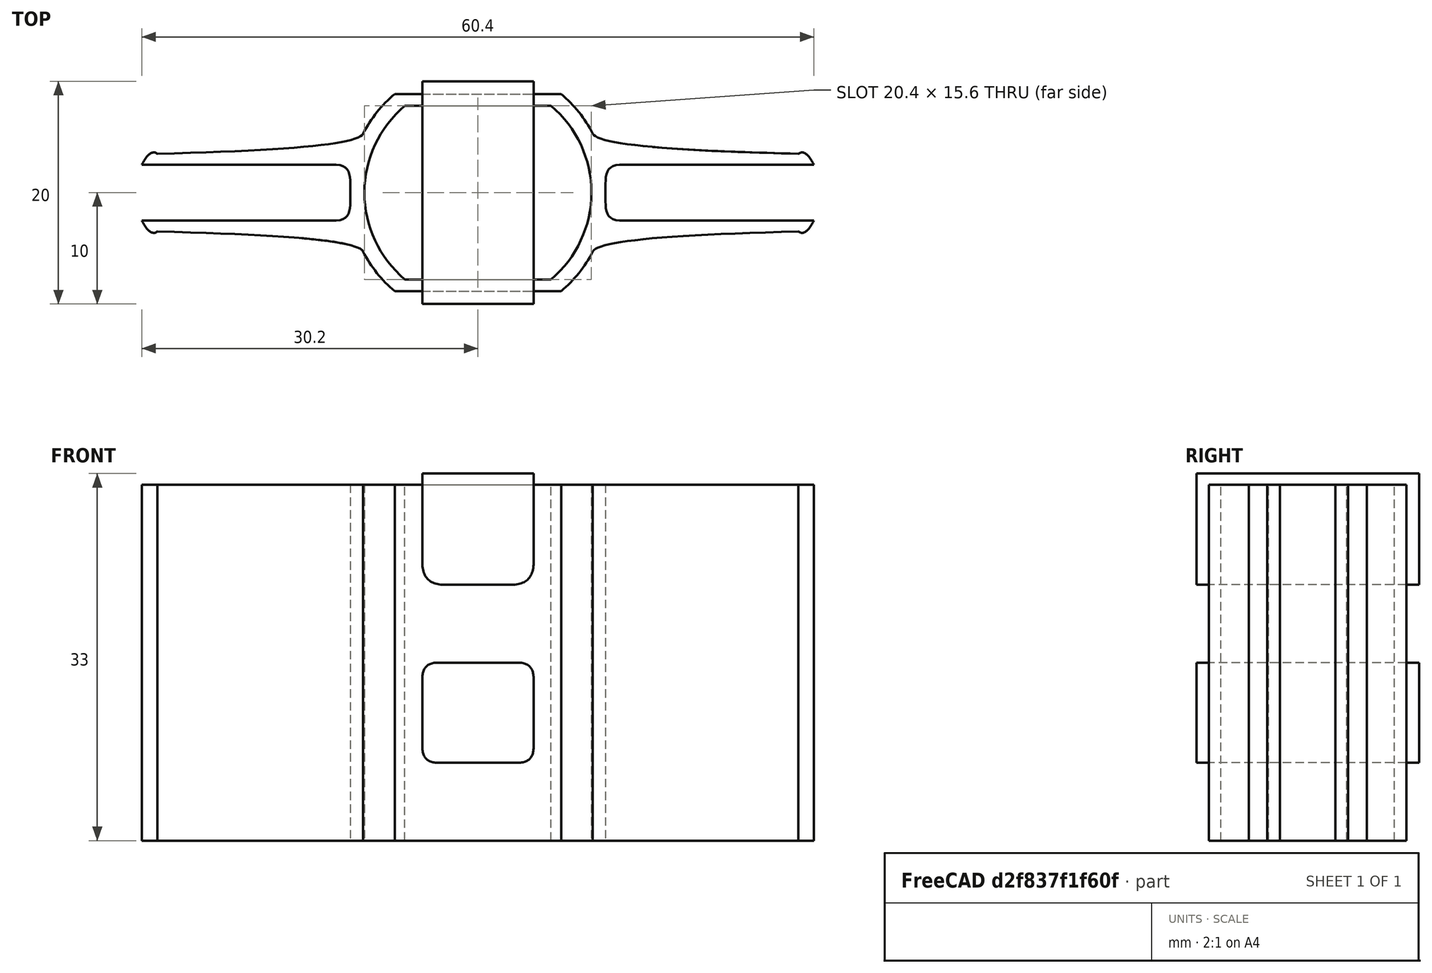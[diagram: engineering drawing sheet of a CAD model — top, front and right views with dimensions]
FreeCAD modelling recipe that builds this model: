
FCSTD DOCUMENT  (FreeCAD 0.19R0.19.2)
Label: 021
License: All rights reserved
LicenseURL: http://en.wikipedia.org/wiki/All_rights_reserved
objects: Sketcher::SketchObject×3, Part::Extrusion×2
note: 5 computed .brp shape members not serialized (recipe doc carries the construction recipe); baked Part::Feature solids carry a one-line shape summary decoded from their .brp

FEATURE [Sketcher::SketchObject] Sketch  label="main001"
  FullyConstrained = true
  sketch-geometry (80):
    g0: ArcOfCircle CenterX=-3.45031e-07 CenterY=0 CenterZ=0 NormalX=0 NormalY=0 NormalZ=1 AngleXU=0 Radius=10.2 StartAngle=5.4126 EndAngle=7.15377
    g1: ArcOfCircle CenterX=-3.45031e-07 CenterY=0 CenterZ=0 NormalX=0 NormalY=0 NormalZ=1 AngleXU=0 Radius=10.2 StartAngle=2.27101 EndAngle=4.01218
    g2: LineSegment StartX=-6.57267 StartY=7.8 StartZ=0 EndX=6.57267 EndY=7.8 EndZ=0
    g3: LineSegment StartX=-6.57267 StartY=-7.8 StartZ=0 EndX=6.57267 EndY=-7.8 EndZ=0
    g4: ArcOfCircle CenterX=-3.45031e-07 CenterY=0 CenterZ=0 NormalX=0 NormalY=0 NormalZ=1 AngleXU=0 Radius=11.6 StartAngle=2.27101 EndAngle=2.66709
    g5: ArcOfCircle CenterX=-3.45031e-07 CenterY=0 CenterZ=0 NormalX=0 NormalY=0 NormalZ=1 AngleXU=0 Radius=11.6 StartAngle=5.4126 EndAngle=5.80868
    g6: LineSegment StartX=-7.4748 StartY=8.87059 StartZ=0 EndX=7.4748 EndY=8.87059 EndZ=0
    g7: LineSegment StartX=-7.4748 StartY=-8.87059 StartZ=0 EndX=7.4748 EndY=-8.87059 EndZ=0
    g8: ArcOfCircle CenterX=-3.45031e-07 CenterY=0 CenterZ=0 NormalX=0 NormalY=0 NormalZ=1 AngleXU=0 Radius=11.6 StartAngle=3.6161 EndAngle=4.01218
    g9: ArcOfCircle CenterX=-3.45031e-07 CenterY=0 CenterZ=0 NormalX=0 NormalY=0 NormalZ=1 AngleXU=0 Radius=11.6 StartAngle=0.474503 EndAngle=0.870585
    g10: Circle CenterX=-28.8 CenterY=3.5 CenterZ=0 NormalX=0 NormalY=0 NormalZ=1 AngleXU=0 Radius=1
    g11: Circle CenterX=-10.9247 CenterY=3.9 CenterZ=0 NormalX=0 NormalY=0 NormalZ=1 AngleXU=0 Radius=1
    g12: Circle CenterX=-10.3184 CenterY=5.3 CenterZ=0 NormalX=0 NormalY=0 NormalZ=1 AngleXU=0 Radius=1
    g13: BSplineCurve PolesCount=3 KnotsCount=2 Degree=2 IsPeriodic=0
    g14: GeomPoint X=-28.8 Y=3.5 Z=0
    g15: GeomPoint X=-10.3184 Y=5.3 Z=0
    g16: Circle CenterX=28.8 CenterY=3.5 CenterZ=0 NormalX=0 NormalY=0 NormalZ=1 AngleXU=0 Radius=1
    g17: Circle CenterX=10.9247 CenterY=3.9 CenterZ=0 NormalX=0 NormalY=0 NormalZ=1 AngleXU=0 Radius=1
    g18: Circle CenterX=10.3184 CenterY=5.3 CenterZ=0 NormalX=0 NormalY=0 NormalZ=1 AngleXU=0 Radius=1
    g19: BSplineCurve PolesCount=3 KnotsCount=2 Degree=2 IsPeriodic=0
    g20: GeomPoint X=28.8 Y=3.5 Z=0
    g21: GeomPoint X=10.3184 Y=5.3 Z=0
    g22: Circle CenterX=-28.8 CenterY=-3.5 CenterZ=0 NormalX=0 NormalY=0 NormalZ=1 AngleXU=0 Radius=1
    g23: Circle CenterX=-10.9247 CenterY=-3.9 CenterZ=0 NormalX=0 NormalY=0 NormalZ=1 AngleXU=0 Radius=1
    g24: Circle CenterX=-10.3184 CenterY=-5.3 CenterZ=0 NormalX=0 NormalY=0 NormalZ=1 AngleXU=0 Radius=1
    g25: BSplineCurve PolesCount=3 KnotsCount=2 Degree=2 IsPeriodic=0
    g26: GeomPoint X=-28.8 Y=-3.5 Z=0
    g27: GeomPoint X=-10.3184 Y=-5.3 Z=0
    g28: Circle CenterX=28.8 CenterY=-3.5 CenterZ=0 NormalX=0 NormalY=0 NormalZ=1 AngleXU=0 Radius=1
    g29: Circle CenterX=10.9247 CenterY=-3.9 CenterZ=0 NormalX=0 NormalY=0 NormalZ=1 AngleXU=0 Radius=1
    g30: Circle CenterX=10.3184 CenterY=-5.3 CenterZ=0 NormalX=0 NormalY=0 NormalZ=1 AngleXU=0 Radius=1
    g31: BSplineCurve PolesCount=3 KnotsCount=2 Degree=2 IsPeriodic=0
    g32: GeomPoint X=28.8 Y=-3.5 Z=0
    g33: GeomPoint X=10.3184 Y=-5.3 Z=0
    g34-g38: Circle x5 (B-spline internal-alignment scaffolding for g39; pole/knot coordinates omitted)
    g39: BSplineCurve PolesCount=5 KnotsCount=3 Degree=3 IsPeriodic=0
    g40: GeomPoint X=12.7274 Y=2.5 Z=0
    g41: GeomPoint X=11.4637 Y=2.49999e-07 Z=0
    g42: GeomPoint X=12.7274 Y=-2.5 Z=0
    g43-g47: Circle x5 (B-spline internal-alignment scaffolding for g48; pole/knot coordinates omitted)
    g48: BSplineCurve PolesCount=5 KnotsCount=3 Degree=3 IsPeriodic=0
    g49: GeomPoint X=-12.7274 Y=2.5 Z=0
    g50: GeomPoint X=-11.4637 Y=2.50004e-07 Z=0
    g51: GeomPoint X=-12.7274 Y=-2.5 Z=0
    g52: LineSegment StartX=-30.2 StartY=-2.5 StartZ=0 EndX=-12.7274 EndY=-2.5 EndZ=0
    g53: LineSegment StartX=-30.2 StartY=2.5 StartZ=0 EndX=-12.7274 EndY=2.5 EndZ=0
    g54: LineSegment StartX=30.2 StartY=2.5 StartZ=0 EndX=12.7274 EndY=2.5 EndZ=0
    g55: LineSegment StartX=30.2 StartY=-2.5 StartZ=0 EndX=12.7274 EndY=-2.5 EndZ=0
    g56: Circle CenterX=-30.2 CenterY=2.5 CenterZ=0 NormalX=0 NormalY=0 NormalZ=1 AngleXU=0 Radius=1
    g57: Circle CenterX=-29.4304 CenterY=3.99253 CenterZ=0 NormalX=0 NormalY=0 NormalZ=1 AngleXU=0 Radius=1
    g58: Circle CenterX=-28.8 CenterY=3.5 CenterZ=0 NormalX=0 NormalY=0 NormalZ=1 AngleXU=0 Radius=1
    g59: BSplineCurve PolesCount=3 KnotsCount=2 Degree=2 IsPeriodic=0
    g60: GeomPoint X=-30.2 Y=2.5 Z=0
    g61: GeomPoint X=-28.8 Y=3.5 Z=0
    g62: Circle CenterX=30.2 CenterY=-2.5 CenterZ=0 NormalX=0 NormalY=0 NormalZ=1 AngleXU=0 Radius=1
    g63: Circle CenterX=29.4304 CenterY=-3.99253 CenterZ=0 NormalX=0 NormalY=0 NormalZ=1 AngleXU=0 Radius=1
    g64: Circle CenterX=28.8 CenterY=-3.5 CenterZ=0 NormalX=0 NormalY=0 NormalZ=1 AngleXU=0 Radius=1
    g65: BSplineCurve PolesCount=3 KnotsCount=2 Degree=2 IsPeriodic=0
    g66: GeomPoint X=30.2 Y=-2.5 Z=0
    g67: GeomPoint X=28.8 Y=-3.5 Z=0
    g68: Circle CenterX=30.2 CenterY=2.5 CenterZ=0 NormalX=0 NormalY=0 NormalZ=1 AngleXU=0 Radius=1
    g69: Circle CenterX=29.4304 CenterY=3.99253 CenterZ=0 NormalX=0 NormalY=0 NormalZ=1 AngleXU=0 Radius=1
    g70: Circle CenterX=28.8 CenterY=3.5 CenterZ=0 NormalX=0 NormalY=0 NormalZ=1 AngleXU=0 Radius=1
    g71: BSplineCurve PolesCount=3 KnotsCount=2 Degree=2 IsPeriodic=0
    g72: GeomPoint X=30.2 Y=2.5 Z=0
    g73: GeomPoint X=28.8 Y=3.5 Z=0
    g74: Circle CenterX=-30.2 CenterY=-2.5 CenterZ=0 NormalX=0 NormalY=0 NormalZ=1 AngleXU=0 Radius=1
    g75: Circle CenterX=-29.4304 CenterY=-3.99253 CenterZ=0 NormalX=0 NormalY=0 NormalZ=1 AngleXU=0 Radius=1
    g76: Circle CenterX=-28.8 CenterY=-3.5 CenterZ=0 NormalX=0 NormalY=0 NormalZ=1 AngleXU=0 Radius=1
    g77: BSplineCurve PolesCount=3 KnotsCount=2 Degree=2 IsPeriodic=0
    g78: GeomPoint X=-30.2 Y=-2.5 Z=0
    g79: GeomPoint X=-28.8 Y=-3.5 Z=0
  constraints (131):
    c: Block(g0)
    c: Equal(g0,g1)
    c: Coincident(g0,g1)
    c: Coincident(g2,g1)
    c: Coincident(g2,g0)
    c: Horizontal(g2)
    c: Coincident(g3,g1)
    c: Coincident(g3,g0)
    c: Horizontal(g3)
    c: Block(g2)
    c: Block(g3)
    c: Coincident(g4,g0)
    c: Coincident(g5,g0)
    c: Block(g5)
    c: Block(g4)
    c: Coincident(g6,g4)
    c: Coincident(g6,g9)
    c: Horizontal(g6)
    c: Coincident(g7,g8)
    c: Coincident(g7,g5)
    c: Horizontal(g7)
    c: Equal(g4,g8)
    c: Coincident(g4,g8)
    c: Equal(g5,g9)
    c: Coincident(g5,g9)
    c: Block(g8)
    c: Block(g9)
    c: Weight(g10) = 1
    c: Equal(g10,g11)
    c: Equal(g10,g12)
    c: Coincident(g13,g4)
    c: InternalAlignment(g10,g13)
    c: InternalAlignment(g11,g13)
    c: InternalAlignment(g12,g13)
    c: InternalAlignment(g14,g13)
    c: InternalAlignment(g15,g13)
    c: Weight(g16) = 1
    c: Equal(g16,g17)
    c: Equal(g16,g18)
    c: Coincident(g19,g9)
    c: InternalAlignment(g16,g19)
    c: InternalAlignment(g17,g19)
    c: InternalAlignment(g18,g19)
    c: InternalAlignment(g20,g19)
    c: InternalAlignment(g21,g19)
    c: Weight(g22) = 1
    c: Equal(g22,g23)
    c: Equal(g22,g24)
    c: Coincident(g25,g8)
    c: InternalAlignment(g22,g25)
    c: InternalAlignment(g23,g25)
    c: InternalAlignment(g24,g25)
    c: InternalAlignment(g26,g25)
    c: InternalAlignment(g27,g25)
    c: Weight(g28) = 1
    c: Equal(g28,g29)
    c: Equal(g28,g30)
    c: Coincident(g31,g5)
    c: InternalAlignment(g28,g31)
    c: InternalAlignment(g29,g31)
    c: InternalAlignment(g30,g31)
    c: InternalAlignment(g32,g31)
    c: InternalAlignment(g33,g31)
    c: Block(g19)
    c: Block(g13)
    c: Block(g31)
    c: Block(g25)
    c: Weight(g34) = 1
    c: Equal(g34, g35-g38) x4
    c: InternalAlignment(g34-g38 -> g39) x5
    c: InternalAlignment(g40,g39)
    c: InternalAlignment(g41,g39)
    c: InternalAlignment(g42,g39)
    c: Weight(g43) = 1
    c: Equal(g43,g44)
    c: Equal(g43,g45)
    c: Equal(g43,g46)
    c: InternalAlignment(g43-g47 -> g48) x5
    c: InternalAlignment(g49,g48)
    c: InternalAlignment(g50,g48)
    c: InternalAlignment(g51,g48)
    c: Block(g48)
    c: Block(g39)
    c: Coincident(g52,g48)
    c: Tangent(g52,g22)
    c: Coincident(g53,g48)
    c: Tangent(g53,g10)
    c: Coincident(g54,g39)
    c: Tangent(g54,g16)
    c: Coincident(g55,g39)
    c: Tangent(g55,g28)
    c: Weight(g56) = 1
    c: Equal(g56,g57)
    c: Equal(g56,g58)
    c: InternalAlignment(g56,g59)
    c: InternalAlignment(g57,g59)
    c: InternalAlignment(g58,g59)
    c: InternalAlignment(g60,g59)
    c: InternalAlignment(g61,g59)
    c: Weight(g62) = 1
    c: Equal(g62,g63)
    c: Equal(g62,g64)
    c: InternalAlignment(g62,g65)
    c: InternalAlignment(g63,g65)
    c: InternalAlignment(g64,g65)
    c: InternalAlignment(g66,g65)
    c: InternalAlignment(g67,g65)
    c: Weight(g68) = 1
    c: Equal(g68,g69)
    c: Equal(g68,g70)
    c: InternalAlignment(g68,g71)
    c: InternalAlignment(g69,g71)
    c: InternalAlignment(g70,g71)
    c: InternalAlignment(g72,g71)
    c: InternalAlignment(g73,g71)
    c: Block(g71)
    c: Block(g54)
    c: Block(g65)
    c: Block(g55)
    c: Weight(g74) = 1
    c: Equal(g74,g75)
    c: Equal(g74,g76)
    c: InternalAlignment(g74,g77)
    c: InternalAlignment(g75,g77)
    c: InternalAlignment(g76,g77)
    c: InternalAlignment(g78,g77)
    c: InternalAlignment(g79,g77)
    c: Block(g77)
    c: Block(g52)
    c: Block(g59)
    c: Block(g53)
FEATURE [Part::Extrusion] Extrude  label="main"
  Base = -> Sketch
  Dir = (0,0,1)
  DirMode = 2
  FaceMakerClass = Part::FaceMakerBullseye
  LengthFwd = 32
  LengthRev = 0
  Solid = true
  Symmetric = false
FEATURE [Sketcher::SketchObject] Sketch001  label="mainCollingAndStructuralHoles"
  FullyConstrained = true
  Placement = pos=(0,0,0) rot=(-1,0,0;4.71239rad)
  sketch-geometry (44):
    g0: Circle CenterX=-5 CenterY=2 CenterZ=0 NormalX=0 NormalY=0 NormalZ=1 AngleXU=0 Radius=1
    g1: Circle CenterX=-5 CenterY=0 CenterZ=0 NormalX=0 NormalY=0 NormalZ=1 AngleXU=0 Radius=1
    g2: Circle CenterX=-3 CenterY=4.6505e-12 CenterZ=0 NormalX=0 NormalY=0 NormalZ=1 AngleXU=0 Radius=1
    g3: BSplineCurve PolesCount=3 KnotsCount=2 Degree=2 IsPeriodic=0
    g4: GeomPoint X=-5 Y=2 Z=0
    g5: GeomPoint X=-3 Y=4.6505e-12 Z=0
    g6: Circle CenterX=5 CenterY=2 CenterZ=0 NormalX=0 NormalY=0 NormalZ=1 AngleXU=0 Radius=1
    g7: Circle CenterX=5 CenterY=4.6505e-12 CenterZ=0 NormalX=0 NormalY=0 NormalZ=1 AngleXU=0 Radius=1
    g8: Circle CenterX=3 CenterY=4.6505e-12 CenterZ=0 NormalX=0 NormalY=0 NormalZ=1 AngleXU=0 Radius=1
    g9: BSplineCurve PolesCount=3 KnotsCount=2 Degree=2 IsPeriodic=0
    g10: GeomPoint X=5 Y=2 Z=0
    g11: GeomPoint X=3 Y=4.6505e-12 Z=0
    g12: LineSegment StartX=5 StartY=2 StartZ=0 EndX=5 EndY=10 EndZ=0
    g13: LineSegment StartX=-5 StartY=2 StartZ=0 EndX=-5 EndY=10 EndZ=0
    g14: LineSegment StartX=-3 StartY=4.6505e-12 StartZ=0 EndX=3 EndY=4.6505e-12 EndZ=0
    g15: LineSegment StartX=-5 StartY=10 StartZ=0 EndX=5 EndY=10 EndZ=0
    g16: Circle CenterX=-3.6 CenterY=-7 CenterZ=0 NormalX=0 NormalY=0 NormalZ=1 AngleXU=0 Radius=1
    g17: Circle CenterX=-5 CenterY=-7 CenterZ=0 NormalX=0 NormalY=0 NormalZ=1 AngleXU=0 Radius=1
    g18: Circle CenterX=-5 CenterY=-8.4 CenterZ=0 NormalX=0 NormalY=0 NormalZ=1 AngleXU=0 Radius=1
    g19: BSplineCurve PolesCount=3 KnotsCount=2 Degree=2 IsPeriodic=0
    g20: GeomPoint X=-3.6 Y=-7 Z=0
    g21: GeomPoint X=-5 Y=-8.4 Z=0
    g22: Circle CenterX=5 CenterY=-8.4 CenterZ=0 NormalX=0 NormalY=0 NormalZ=1 AngleXU=0 Radius=1
    g23: Circle CenterX=5 CenterY=-7 CenterZ=0 NormalX=0 NormalY=0 NormalZ=1 AngleXU=0 Radius=1
    g24: Circle CenterX=3.6 CenterY=-7 CenterZ=0 NormalX=0 NormalY=0 NormalZ=1 AngleXU=0 Radius=1
    g25: BSplineCurve PolesCount=3 KnotsCount=2 Degree=2 IsPeriodic=0
    g26: GeomPoint X=5 Y=-8.4 Z=0
    g27: GeomPoint X=3.6 Y=-7 Z=0
    g28: Circle CenterX=-3.6 CenterY=-16 CenterZ=0 NormalX=0 NormalY=0 NormalZ=1 AngleXU=0 Radius=1
    g29: Circle CenterX=-5 CenterY=-16 CenterZ=0 NormalX=0 NormalY=0 NormalZ=1 AngleXU=0 Radius=1
    g30: Circle CenterX=-5 CenterY=-14.6 CenterZ=0 NormalX=0 NormalY=0 NormalZ=1 AngleXU=0 Radius=1
    g31: BSplineCurve PolesCount=3 KnotsCount=2 Degree=2 IsPeriodic=0
    g32: GeomPoint X=-3.6 Y=-16 Z=0
    g33: GeomPoint X=-5 Y=-14.6 Z=0
    g34: Circle CenterX=5 CenterY=-14.6 CenterZ=0 NormalX=0 NormalY=0 NormalZ=1 AngleXU=0 Radius=1
    g35: Circle CenterX=5 CenterY=-16 CenterZ=0 NormalX=0 NormalY=0 NormalZ=1 AngleXU=0 Radius=1
    g36: Circle CenterX=3.6 CenterY=-16 CenterZ=0 NormalX=0 NormalY=0 NormalZ=1 AngleXU=0 Radius=1
    g37: BSplineCurve PolesCount=3 KnotsCount=2 Degree=2 IsPeriodic=0
    g38: GeomPoint X=5 Y=-14.6 Z=0
    g39: GeomPoint X=3.6 Y=-16 Z=0
    g40: LineSegment StartX=-3.6 StartY=-7 StartZ=0 EndX=3.6 EndY=-7 EndZ=0
    g41: LineSegment StartX=-5 StartY=-8.4 StartZ=0 EndX=-5 EndY=-14.6 EndZ=0
    g42: LineSegment StartX=-3.6 StartY=-16 StartZ=0 EndX=3.6 EndY=-16 EndZ=0
    g43: LineSegment StartX=5 StartY=-14.6 StartZ=0 EndX=5 EndY=-8.4 EndZ=0
  constraints (79):
    c: Weight(g0) = 1
    c: Equal(g0,g1)
    c: Equal(g0,g2)
    c: InternalAlignment(g0,g3)
    c: InternalAlignment(g1,g3)
    c: InternalAlignment(g2,g3)
    c: InternalAlignment(g4,g3)
    c: InternalAlignment(g5,g3)
    c: Weight(g6) = 1
    c: Equal(g6,g7)
    c: Equal(g6,g8)
    c: InternalAlignment(g6,g9)
    c: InternalAlignment(g7,g9)
    c: InternalAlignment(g8,g9)
    c: InternalAlignment(g10,g9)
    c: InternalAlignment(g11,g9)
    c: Block(g3)
    c: Coincident(g13,g3)
    c: Block(g9)
    c: Coincident(g12,g9)
    c: Vertical(g12)
    c: Block(g12)
    c: Block(g13)
    c: Coincident(g14,g3)
    c: Coincident(g14,g9)
    c: Horizontal(g14)
    c: Coincident(g15,g13)
    c: Coincident(g15,g12)
    c: Horizontal(g15)
    c: Distance(g12) = 8
    c: Distance(g15) = 10
    c: Weight(g16) = 1
    c: Equal(g16,g17)
    c: Equal(g16,g18)
    c: InternalAlignment(g16,g19)
    c: InternalAlignment(g17,g19)
    c: InternalAlignment(g18,g19)
    c: InternalAlignment(g20,g19)
    c: InternalAlignment(g21,g19)
    c: Weight(g22) = 1
    c: Equal(g22,g23)
    c: Equal(g22,g24)
    c: InternalAlignment(g22,g25)
    c: InternalAlignment(g23,g25)
    c: InternalAlignment(g24,g25)
    c: InternalAlignment(g26,g25)
    c: InternalAlignment(g27,g25)
    c: Weight(g28) = 1
    c: Equal(g28,g29)
    c: Equal(g28,g30)
    c: InternalAlignment(g28,g31)
    c: InternalAlignment(g29,g31)
    c: InternalAlignment(g30,g31)
    c: InternalAlignment(g32,g31)
    c: InternalAlignment(g33,g31)
    c: Weight(g34) = 1
    c: Equal(g34,g35)
    c: Equal(g34,g36)
    c: InternalAlignment(g34,g37)
    c: InternalAlignment(g35,g37)
    c: InternalAlignment(g36,g37)
    c: InternalAlignment(g38,g37)
    c: InternalAlignment(g39,g37)
    c: Block(g25)
    c: Block(g37)
    c: Block(g31)
    c: Block(g19)
    c: Coincident(g40,g19)
    c: Coincident(g40,g25)
    c: Horizontal(g40)
    c: Coincident(g41,g19)
    c: Coincident(g41,g31)
    c: Vertical(g41)
    c: Coincident(g42,g31)
    c: Coincident(g42,g37)
    c: Horizontal(g42)
    c: Coincident(g43,g37)
    c: Coincident(g43,g25)
    c: Vertical(g43)
FEATURE [Part::Extrusion] Extrude001  label="mainCollingAndStructuralHoles001"
  Base = -> Sketch001
  Dir = (0,-1,3e-16)
  DirMode = 2
  FaceMakerClass = Part::FaceMakerBullseye
  LengthFwd = 20
  LengthRev = 0
  Placement = pos=(0,10,23) rot=(0,0,1;0rad)
  Solid = true
  Symmetric = false
FEATURE [Sketcher::SketchObject] Sketch002
  FullyConstrained = true
  Placement = pos=(0,0,0) rot=(-1,0,0;4.71239rad)
  sketch-geometry (12):
    g0: LineSegment StartX=0 StartY=0 StartZ=0 EndX=-12.73 EndY=0 EndZ=0
    g1: LineSegment StartX=-12.73 StartY=0 StartZ=0 EndX=-28.43 EndY=0 EndZ=0
    g2: LineSegment StartX=-28.43 StartY=0 StartZ=0 EndX=-28.43 EndY=3 EndZ=0
    g3: LineSegment StartX=-28.43 StartY=3 StartZ=0 EndX=-28.43 EndY=4.4 EndZ=0
    g4: LineSegment StartX=-28.43 StartY=3 StartZ=0 EndX=-27.03 EndY=3 EndZ=0
    g5: LineSegment StartX=-28.43 StartY=13.1 StartZ=0 EndX=-28.43 EndY=4.4 EndZ=0
    g6: LineSegment StartX=-28.43 StartY=13.1 StartZ=0 EndX=-28.43 EndY=14.5 EndZ=0
    g7: LineSegment StartX=-28.43 StartY=17.5 StartZ=0 EndX=-28.43 EndY=14.5 EndZ=0
    g8: LineSegment StartX=-28.43 StartY=27.6 StartZ=0 EndX=-28.43 EndY=29 EndZ=0
    g9: LineSegment StartX=-28.43 StartY=27.6 StartZ=0 EndX=-28.43 EndY=18.9 EndZ=0
    g10: LineSegment StartX=-28.43 StartY=17.5 StartZ=0 EndX=-27.03 EndY=17.5 EndZ=0
    g11: LineSegment StartX=-28.43 StartY=17.5 StartZ=0 EndX=-28.43 EndY=18.9 EndZ=0
  constraints (36):
    c: Coincident(g0,g-1)
    c: Horizontal(g0)
    c: Distance(g0) = 12.73
    c: Coincident(g1,g0)
    c: Horizontal(g1)
    c: Distance(g1) = 15.7
    c: Coincident(g2,g1)
    c: Vertical(g2)
    c: Distance(g2) = 3
    c: Coincident(g3,g2)
    c: Vertical(g3)
    c: Distance(g3) = 1.4
    c: Coincident(g4,g2)
    c: Horizontal(g4)
    c: Distance(g4) = 1.4
    c: Distance(g5) = 8.7
    c: Vertical(g5)
    c: Coincident(g5,g3)
    c: Vertical(g6)
    c: Equal(g3,g6) = 1.4
    c: Coincident(g6,g5)
    c: Vertical(g7)
    c: Distance(g7) = 3
    c: Coincident(g7,g6)
    c: Vertical(g11)
    c: Equal(g3,g11) = 1.4
    c: Horizontal(g10)
    c: Equal(g4,g10) = 1.4
    c: Equal(g5,g9) = 8.7
    c: Vertical(g9)
    c: Coincident(g9,g11)
    c: Vertical(g8)
    c: Equal(g11,g8) = 1.4
    c: Coincident(g8,g9)
    c: Coincident(g11,g7)
    c: Block(g10)
